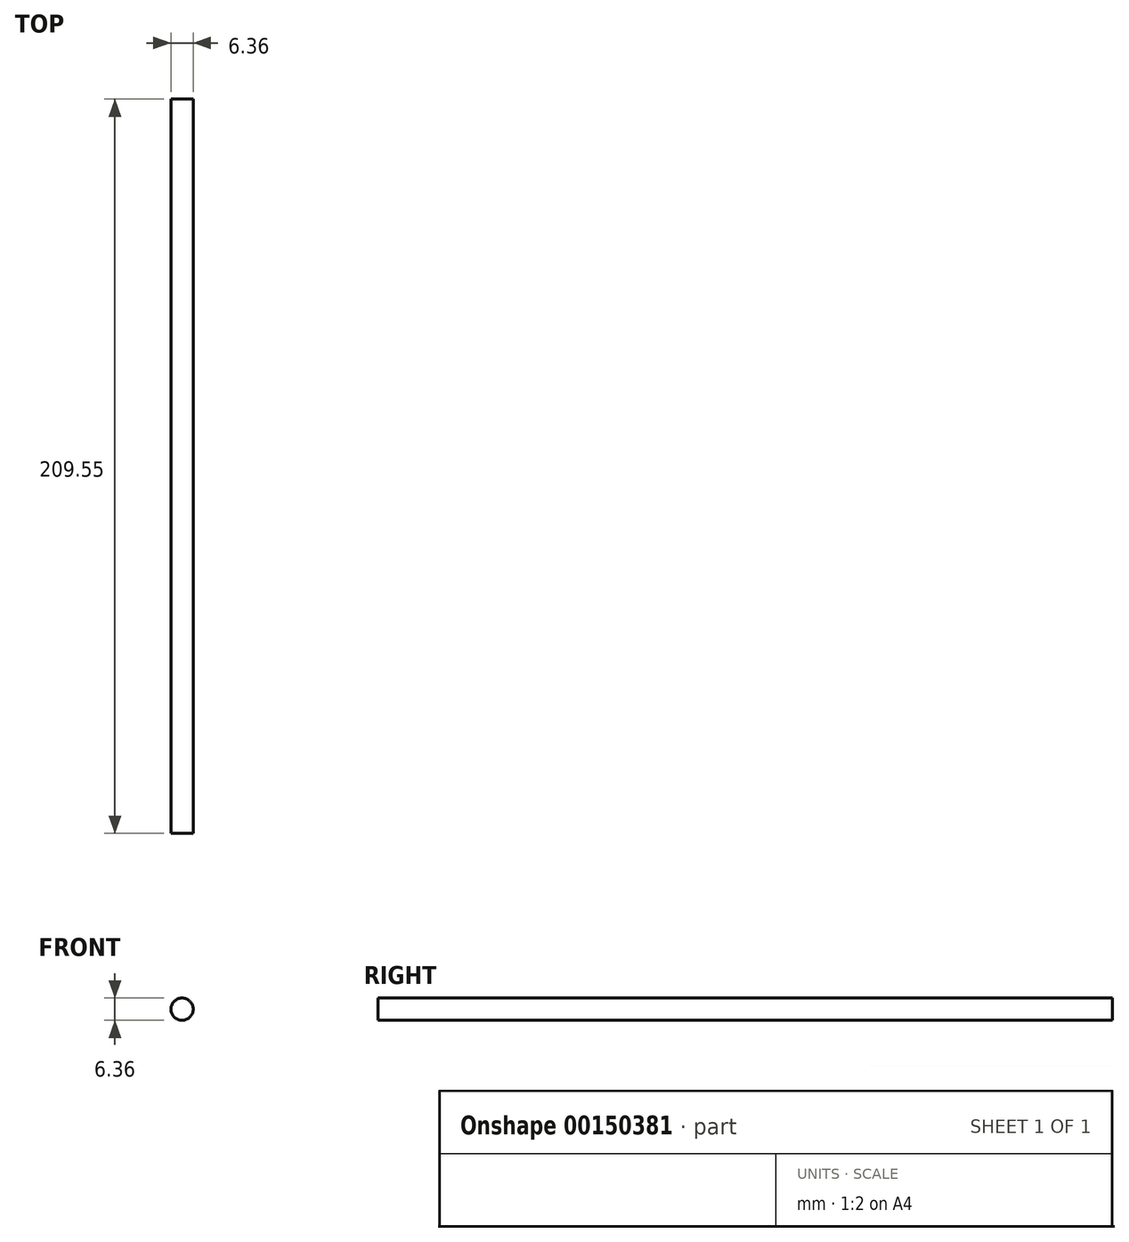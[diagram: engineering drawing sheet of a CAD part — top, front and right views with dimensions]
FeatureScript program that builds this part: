
annotation { "Feature Type Name" : "Feature", "Feature Type Description" : "" }
export const myFeature = defineFeature(function(context is Context, id is Id, definition is map)
    precondition{}
    {
        {
            var Q0;
            Q0=qCreatedBy(makeId("Front.planeOp"),FACE);
            var sketch = newSketch(context, id + "F0", { "sketchPlane" : qUnion([Q0])});
            skCircle(sketch, "E0", {"center": v(0, 0) * mm, "radius": 3.18 * mm});
            skSolve(sketch);
        }
        {
            var Q0;
            Q0 = qSketchRegion(id + "F0", true);
            extrude(context, id + "F1", {"entities" : qUnion([Q0]), "depth" : 209.55 * mm});
        }
    });
